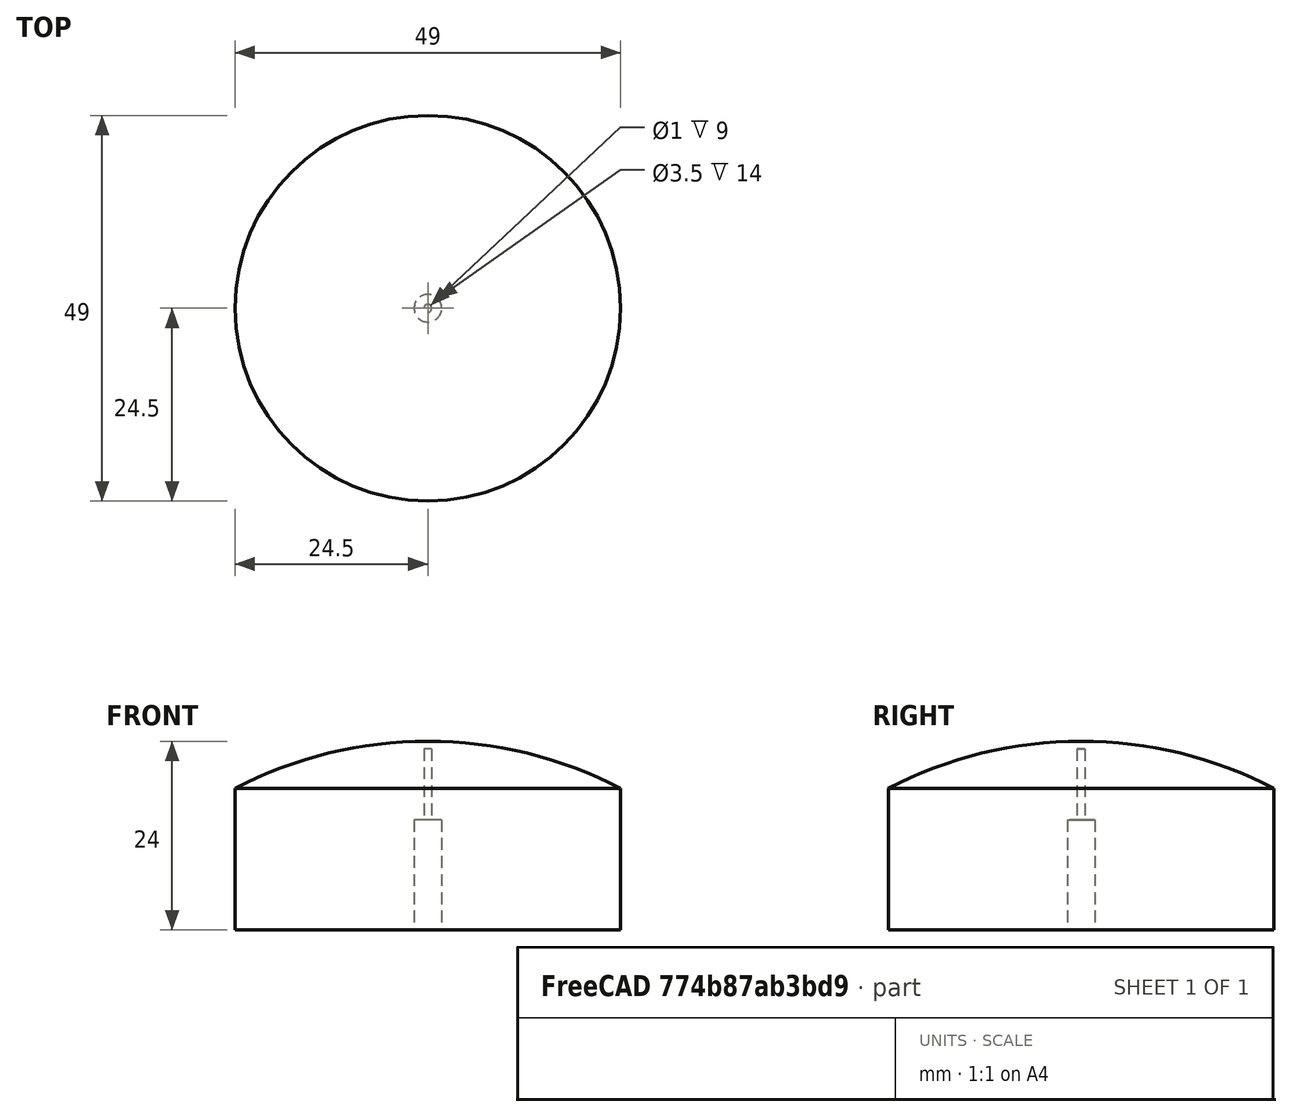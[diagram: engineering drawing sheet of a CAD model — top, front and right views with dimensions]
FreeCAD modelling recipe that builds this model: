
FCSTD DOCUMENT  (FreeCAD 0.19R24291 (Git))
Label: ToyWheel
License: All rights reserved
LicenseURL: http://en.wikipedia.org/wiki/All_rights_reserved
objects: Mesh::Feature×1, Sketcher::SketchObject×1, PartDesign::Revolution×1, PartDesign::Body×1
note: 4 computed .brp shape members not serialized (recipe doc carries the construction recipe); baked Part::Feature solids carry a one-line shape summary decoded from their .brp

FEATURE [Mesh::Feature] ToyWheel
FEATURE [Sketcher::SketchObject] Sketch
  FullyConstrained = true
  MapMode = 5
  Placement = pos=(0,0,0) rot=(1,0,0;1.5708rad)
  Support = -> [XZ_Plane]
  sketch-geometry (8):
    g0: LineSegment StartX=0 StartY=23 StartZ=0 EndX=0.5 EndY=23 EndZ=0
    g1: LineSegment StartX=0.5 StartY=23 StartZ=0 EndX=0.5 EndY=14 EndZ=0
    g2: LineSegment StartX=0.5 StartY=14 StartZ=0 EndX=1.75 EndY=14 EndZ=0
    g3: LineSegment StartX=1.75 StartY=14 StartZ=0 EndX=1.75 EndY=0 EndZ=0
    g4: LineSegment StartX=1.75 StartY=0 StartZ=0 EndX=24.5 EndY=0 EndZ=0
    g5: LineSegment StartX=24.5 StartY=0 StartZ=0 EndX=24.5 EndY=18 EndZ=0
    g6: LineSegment StartX=0 StartY=23 StartZ=0 EndX=3.2e-15 EndY=24 EndZ=0
    g7: ArcOfCircle CenterX=0 CenterY=-29.0208 CenterZ=0 NormalX=0 NormalY=0 NormalZ=1 AngleXU=0 Radius=53.0208 StartAngle=1.09045 EndAngle=1.5708
  constraints (25):
    c: PointOnObject(g0,g-2)
    c: Horizontal(g0)
    c: Coincident(g0,g1)
    c: Vertical(g1)
    c: Coincident(g1,g2)
    c: Horizontal(g2)
    c: Coincident(g2,g3)
    c: PointOnObject(g3,g-1)
    c: Vertical(g3)
    c: Coincident(g3,g4)
    c: PointOnObject(g4,g-1)
    c: Coincident(g4,g5)
    c: Vertical(g5)
    c: Coincident(g0,g6)
    c: PointOnObject(g6,g-2)
    c: PointOnObject(g7,g-2)
    c: Coincident(g7,g6)
    c: Coincident(g7,g5)
    c: Distance(g-1,g6) = 24
    c: DistanceX(g5) = 24.5
    c: DistanceY(g5) = 18
    c: Distance(g6) = 1
    c: Distance(g3,g-1) = 1.75
    c: Distance(g3) = 14
    c: Distance(g1,g-2) = 0.5
FEATURE [PartDesign::Revolution] Revolution
  Angle = 360
  Axis = (0,2e-16,1)
  Base = (0,0,0)
  Placement = pos=(0,0,0) rot=(1,0,0;1.5708rad)
  Profile = -> Sketch
  ReferenceAxis = -> Sketch [V_Axis]
  Reversed = true
FEATURE [PartDesign::Body] Body
  Group = -> [Sketch,Revolution]
  Origin = -> Origin
  Tip = -> Revolution
